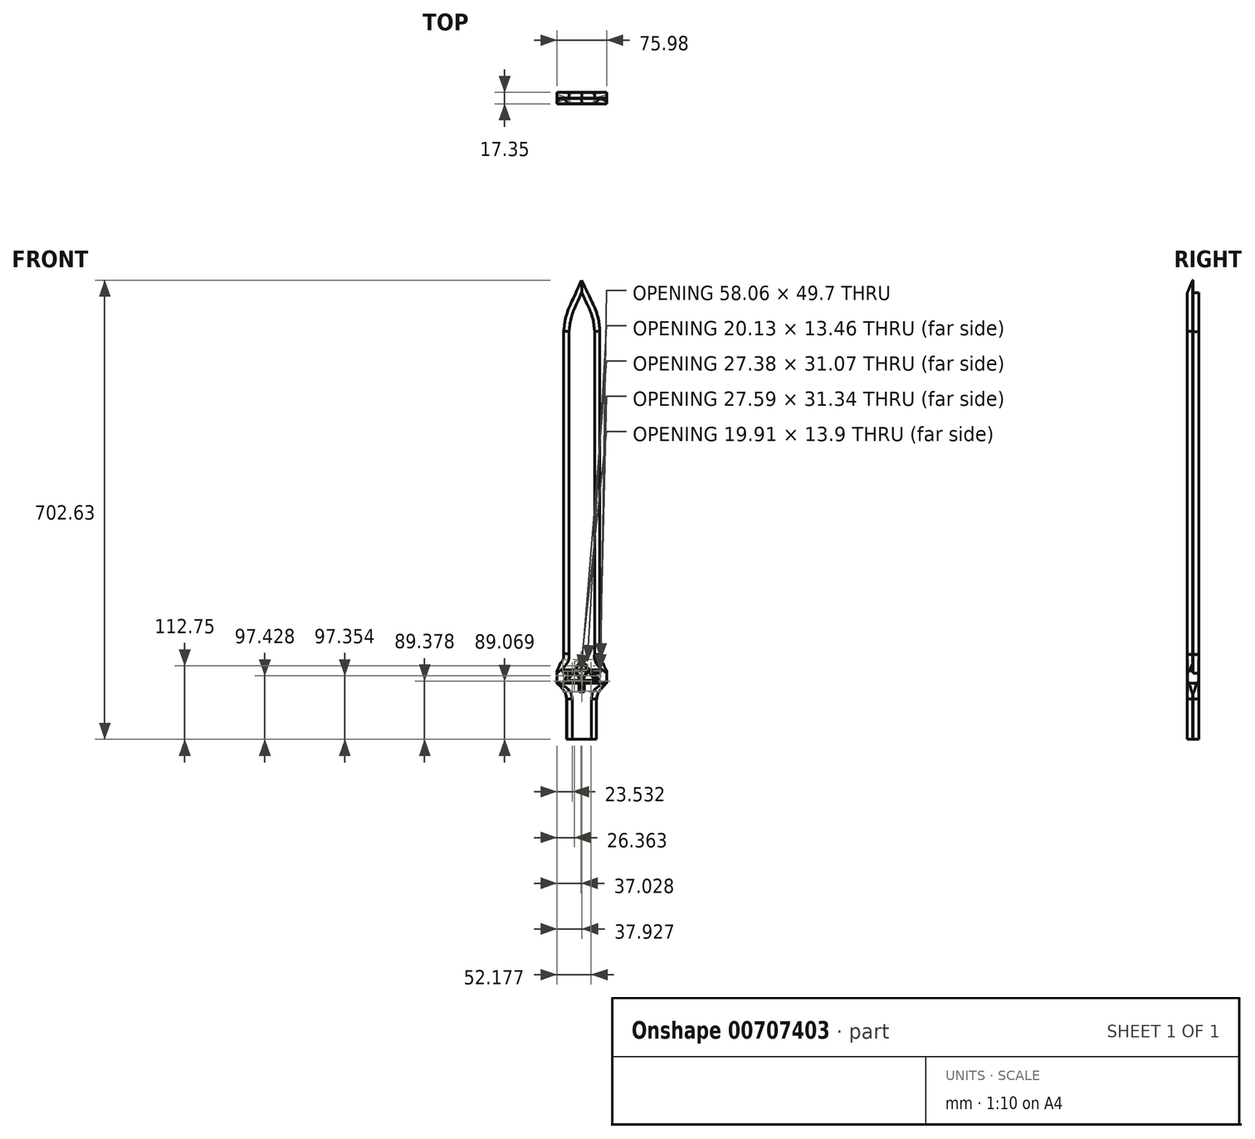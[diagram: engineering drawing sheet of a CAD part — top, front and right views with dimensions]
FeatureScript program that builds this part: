
annotation { "Feature Type Name" : "Feature", "Feature Type Description" : "" }
export const myFeature = defineFeature(function(context is Context, id is Id, definition is map)
    precondition{}
    {
        {
            var Q0;
            Q0=qCreatedBy(makeId("Front.planeOp"),FACE);
            var sketch = newSketch(context, id + "F0", { "sketchPlane" : qUnion([Q0])});
            skLineSegment(sketch, "E0", {"start": v(-23.18, 89.36) * mm, "end": v(-23.18, 27.94) * mm});
            skLineSegment(sketch, "E1", {"start": v(-23.18, 27.94) * mm, "end": v(22.75, 27.94) * mm});
            skLineSegment(sketch, "E2", {"start": v(22.75, 27.94) * mm, "end": v(22.75, 89.36) * mm});
            skFitSpline(sketch, "E3", {"points": [v(-23.18, 89.36) * mm, v(-25.2, 98.78) * mm, v(-29.58, 105.34) * mm, v(-34.12, 110.56) * mm, v(-37.82, 114.26) * mm], "startDerivative": vector(-4.45, 34.79) * mm, "endDerivative": vector(-17.26, 16.67) * mm});
            skFitSpline(sketch, "E4", {"points": [v(22.75, 89.36) * mm, v(24.94, 98.27) * mm, v(29.82, 105.5) * mm, v(34.53, 110.56) * mm, v(38.16, 114.22) * mm], "startDerivative": vector(5.26, 33.12) * mm, "endDerivative": vector(16.94, 16.97) * mm});
            skLineSegment(sketch, "E5", {"start": v(-37.82, 114.26) * mm, "end": v(-37.82, 132.92) * mm});
            skLineSegment(sketch, "E6", {"start": v(38.16, 114.22) * mm, "end": v(38.16, 132.92) * mm});
            skFitSpline(sketch, "E7", {"points": [v(-37.82, 132.92) * mm, v(-34.87, 138.92) * mm, v(-32.96, 144.16) * mm, v(-31.8, 152.09) * mm, v(-31.68, 159) * mm], "startDerivative": vector(12.58, 24.9) * mm, "endDerivative": vector(-0.2, 26.4) * mm});
            skFitSpline(sketch, "E8", {"points": [v(38.16, 132.92) * mm, v(35.43, 137.9) * mm, v(32.87, 144.8) * mm, v(31.98, 152.47) * mm, v(31.85, 157.97) * mm], "startDerivative": vector(-11.86, 20.42) * mm, "endDerivative": vector(-0.27, 22.84) * mm});
            skLineSegment(sketch, "E9", {"start": v(-31.68, 159) * mm, "end": v(-31.68, 655.53) * mm});
            skLineSegment(sketch, "E10", {"start": v(31.85, 157.97) * mm, "end": v(31.87, 655.53) * mm});
            skFitSpline(sketch, "E11", {"points": [v(0, 770.67) * mm, v(5.75, 755.45) * mm, v(13.9, 732.8) * mm, v(20.44, 712.09) * mm, v(27.87, 687.66) * mm, v(30.7, 671.38) * mm, v(31.87, 655.53) * mm], "startDerivative": vector(35.97, -94.67) * mm, "endDerivative": vector(6.36, -107.63) * mm});
            skFitSpline(sketch, "E12", {"points": [v(0, 770.67) * mm, v(-7.17, 751.02) * mm, v(-17.08, 723.77) * mm, v(-25.22, 697.22) * mm, v(-28.94, 682) * mm, v(-31.68, 655.53) * mm], "startDerivative": vector(-36.3, -100.65) * mm, "endDerivative": vector(-10.82, -136.16) * mm});
            skSolve(sketch);
        }
        {
            var Q0;
            Q0=makeQuery(id+"F0.imprint","IMPRINT",FACE,{"disambiguationData":[TD([[makeQuery(id+"F0.imprint","IMPRINT",EDGE,{"derivedFrom":sQuery(id+"F0.wireOp",EDGE,"E0")}),1.0]])]});
            extrude(context, id + "F1", {"entities" : qUnion([Q0]), "depth" : 0.25 * mm, "offsetDistance" : 25.4 * mm});
        }
        {
            var Q0;
            Q0=makeQuery(id+"F1.opExtrude","CAP_FACE",FACE,{"disambiguationData":[OSD([sQuery(id+"F0.wireOp",EDGE,"E0"),sQuery(id+"F0.wireOp",EDGE,"E1"),sQuery(id+"F0.wireOp",EDGE,"E2"),sQuery(id+"F0.wireOp",EDGE,"E3"),sQuery(id+"F0.wireOp",EDGE,"E4"),sQuery(id+"F0.wireOp",EDGE,"E5"),sQuery(id+"F0.wireOp",EDGE,"E6"),sQuery(id+"F0.wireOp",EDGE,"E7"),sQuery(id+"F0.wireOp",EDGE,"E8"),sQuery(id+"F0.wireOp",EDGE,"E9"),sQuery(id+"F0.wireOp",EDGE,"E10"),sQuery(id+"F0.wireOp",EDGE,"E11"),sQuery(id+"F0.wireOp",EDGE,"E12")])],"isStart":true});
            extrude(context, id + "F2", {"entities" : qUnion([Q0]), "operationType" : NewBodyOperationType.ADD, "depth" : 0.25 * mm, "offsetDistance" : 25.4 * mm});
        }
        {
            var Q0;
            Q0=makeQuery(id+"F2.opExtrude","CAP_FACE",FACE,{"disambiguationData":[OSD([sQuery(id+"F0.wireOp",EDGE,"E0"),sQuery(id+"F0.wireOp",EDGE,"E1"),sQuery(id+"F0.wireOp",EDGE,"E2"),sQuery(id+"F0.wireOp",EDGE,"E3"),sQuery(id+"F0.wireOp",EDGE,"E4"),sQuery(id+"F0.wireOp",EDGE,"E5"),sQuery(id+"F0.wireOp",EDGE,"E6"),sQuery(id+"F0.wireOp",EDGE,"E7"),sQuery(id+"F0.wireOp",EDGE,"E8"),sQuery(id+"F0.wireOp",EDGE,"E9"),sQuery(id+"F0.wireOp",EDGE,"E10"),sQuery(id+"F0.wireOp",EDGE,"E11"),sQuery(id+"F0.wireOp",EDGE,"E12")])],"isStart":false});
            var sketch = newSketch(context, id + "F3", { "sketchPlane" : qUnion([Q0])});
            skLineSegment(sketch, "E13", {"start": v(-14.88, 27.94) * mm, "end": v(-14.88, 90.23) * mm});
            skFitSpline(sketch, "E14", {"points": [v(-14.88, 90.23) * mm, v(-16.73, 99.87) * mm, v(-22.43, 106.47) * mm, v(-31.13, 113.07) * mm, v(-38.16, 117.57) * mm], "startDerivative": vector(-3.35, 40.52) * mm, "endDerivative": vector(-28.93, 17.8) * mm});
            skLineSegment(sketch, "E15", {"start": v(14.47, 27.94) * mm, "end": v(14.47, 90.23) * mm});
            skFitSpline(sketch, "E16", {"points": [v(14.47, 90.23) * mm, v(16.95, 99.87) * mm, v(22.69, 106.47) * mm, v(31.86, 113.07) * mm, v(37.82, 117.57) * mm], "startDerivative": vector(6.55, 39.9) * mm, "endDerivative": vector(24.56, 19.23) * mm});
            skFitSpline(sketch, "E17", {"points": [v(37.82, 129.66) * mm, v(28.49, 136.84) * mm, v(22.69, 144.12) * mm, v(19.73, 151.4) * mm, v(19.42, 158.88) * mm], "startDerivative": vector(-34.92, 24.3) * mm, "endDerivative": vector(1.06, 33.21) * mm});
            skFitSpline(sketch, "E18", {"points": [v(-38.16, 129.14) * mm, v(-30.17, 135.78) * mm, v(-23.73, 142.32) * mm, v(-20.88, 147.8) * mm, v(-19.51, 153.3) * mm, v(-19.62, 158.04) * mm], "startDerivative": vector(33.35, 27.05) * mm, "endDerivative": vector(-2.46, 28.44) * mm});
            skLineSegment(sketch, "E19", {"start": v(-19.62, 158.04) * mm, "end": v(-19.62, 652.03) * mm});
            skLineSegment(sketch, "E20", {"start": v(19.42, 158.88) * mm, "end": v(19.33, 652.03) * mm});
            skFitSpline(sketch, "E21", {"points": [v(19.33, 652.03) * mm, v(15.9, 673.87) * mm, v(8.12, 693.88) * mm, v(0, 711.54) * mm], "startDerivative": vector(-6.72, 64.73) * mm, "endDerivative": vector(-25.08, 54.21) * mm});
            skFitSpline(sketch, "E22", {"points": [v(-19.62, 652.03) * mm, v(-16.6, 673.4) * mm, v(-8.12, 694.59) * mm, v(0, 711.54) * mm], "startDerivative": vector(4.95, 63.37) * mm, "endDerivative": vector(25.12, 52.1) * mm});
            skSolve(sketch);
        }
        {
            var Q0;
            {var subQ4=sQuery(id+"F3.wireOp",EDGE,"E13");Q0=makeQuery(id+"F3.imprint","IMPRINT",FACE,{"disambiguationData":[TD([[makeQuery(id+"F3.imprint","IMPRINT",EDGE,{"derivedFrom":subQ4}),-1.0]])]});}
            extrude(context, id + "F4", {"entities" : qUnion([Q0]), "operationType" : NewBodyOperationType.ADD, "depth" : 12.7 * mm, "offsetDistance" : 25.4 * mm});
        }
        {
            var Q0;
            Q0=makeQuery(id+"F4.opExtrude","CAP_FACE",FACE,{"disambiguationData":[OSD([sQuery(id+"F0.wireOp",EDGE,"E1"),sQuery(id+"F0.wireOp",EDGE,"E5"),sQuery(id+"F0.wireOp",EDGE,"E6"),sQuery(id+"F3.wireOp",EDGE,"E13"),sQuery(id+"F3.wireOp",EDGE,"E14"),sQuery(id+"F3.wireOp",EDGE,"E15"),sQuery(id+"F3.wireOp",EDGE,"E16"),sQuery(id+"F3.wireOp",EDGE,"E17"),sQuery(id+"F3.wireOp",EDGE,"E18"),sQuery(id+"F3.wireOp",EDGE,"E19"),sQuery(id+"F3.wireOp",EDGE,"E20"),sQuery(id+"F3.wireOp",EDGE,"E21"),sQuery(id+"F3.wireOp",EDGE,"E22")])],"isStart":false});
            extrude(context, id + "F5", {"entities" : qUnion([Q0]), "operationType" : NewBodyOperationType.ADD, "oppositeDirection" : true, "depth" : 25.9 * mm, "offsetDistance" : 25.4 * mm});
        }
        {
            var Q0;
            Q0=makeQuery(id+"F4.opExtrude","CAP_EDGE",EDGE,{"disambiguationData":[OSD([sQuery(id+"F3.wireOp",EDGE,"E22")])],"isStart":true});
            var Q1;
            Q1=makeQuery(id+"F4.opExtrude","CAP_EDGE",EDGE,{"disambiguationData":[OSD([sQuery(id+"F3.wireOp",EDGE,"E19")])],"isStart":true});
            var Q2;
            Q2=makeQuery(id+"F4.opExtrude","CAP_EDGE",EDGE,{"disambiguationData":[OSD([sQuery(id+"F3.wireOp",EDGE,"E21")])],"isStart":true});
            var Q3;
            Q3=makeQuery(id+"F4.opExtrude","CAP_EDGE",EDGE,{"disambiguationData":[OSD([sQuery(id+"F3.wireOp",EDGE,"E20")])],"isStart":true});
            var Q4;
            Q4=makeQuery(id+"F4.opExtrude","CAP_EDGE",EDGE,{"disambiguationData":[OSD([sQuery(id+"F3.wireOp",EDGE,"E17")])],"isStart":true});
            var Q5;
            Q5=makeQuery(id+"F4.opExtrude","CAP_EDGE",EDGE,{"disambiguationData":[OSD([sQuery(id+"F3.wireOp",EDGE,"E18")])],"isStart":true});
            var Q6;
            Q6=makeQuery(id+"F4.opExtrude","CAP_EDGE",EDGE,{"disambiguationData":[OSD([sQuery(id+"F3.wireOp",EDGE,"E14")])],"isStart":true});
            var Q7;
            Q7=makeQuery(id+"F4.opExtrude","CAP_EDGE",EDGE,{"disambiguationData":[OSD([sQuery(id+"F3.wireOp",EDGE,"E16")])],"isStart":true});
            var Q8;
            Q8=makeQuery(id+"F4.opExtrude","CAP_EDGE",EDGE,{"disambiguationData":[OSD([sQuery(id+"F3.wireOp",EDGE,"E15")])],"isStart":true});
            var Q9;
            Q9=makeQuery(id+"F4.opExtrude","CAP_EDGE",EDGE,{"disambiguationData":[OSD([sQuery(id+"F3.wireOp",EDGE,"E13")])],"isStart":true});
            chamfer(context, id + "F6", {"entities" : qUnion([Q0, Q1, Q2, Q3, Q4, Q5, Q6, Q7, Q8, Q9]), "chamferType" : ChamferType.OFFSET_ANGLE, "width" : 8.13 * mm, "oppositeDirection" : false, "angle" : 47 * degree, "tangentPropagation" : true});
        }
        {
            var Q0;
            Q0=makeQuery(id+"F5.boolean.opBoolean","INTERSECT",EDGE,{"derivedFrom":[makeQuery(id+"F1.opExtrude","CAP_FACE",FACE,{"disambiguationData":[OSD([sQuery(id+"F0.wireOp",EDGE,"E0"),sQuery(id+"F0.wireOp",EDGE,"E1"),sQuery(id+"F0.wireOp",EDGE,"E2"),sQuery(id+"F0.wireOp",EDGE,"E3"),sQuery(id+"F0.wireOp",EDGE,"E4"),sQuery(id+"F0.wireOp",EDGE,"E5"),sQuery(id+"F0.wireOp",EDGE,"E6"),sQuery(id+"F0.wireOp",EDGE,"E7"),sQuery(id+"F0.wireOp",EDGE,"E8"),sQuery(id+"F0.wireOp",EDGE,"E9"),sQuery(id+"F0.wireOp",EDGE,"E10"),sQuery(id+"F0.wireOp",EDGE,"E11"),sQuery(id+"F0.wireOp",EDGE,"E12")])],"isStart":false}),makeQuery(id+"F5.opExtrude","SWEPT_FACE",FACE,{"disambiguationData":[OSD([sQuery(id+"F3.wireOp",EDGE,"E20")])]})]});
            var Q1;
            Q1=makeQuery(id+"F5.boolean.opBoolean","INTERSECT",EDGE,{"derivedFrom":[makeQuery(id+"F1.opExtrude","CAP_FACE",FACE,{"disambiguationData":[OSD([sQuery(id+"F0.wireOp",EDGE,"E0"),sQuery(id+"F0.wireOp",EDGE,"E1"),sQuery(id+"F0.wireOp",EDGE,"E2"),sQuery(id+"F0.wireOp",EDGE,"E3"),sQuery(id+"F0.wireOp",EDGE,"E4"),sQuery(id+"F0.wireOp",EDGE,"E5"),sQuery(id+"F0.wireOp",EDGE,"E6"),sQuery(id+"F0.wireOp",EDGE,"E7"),sQuery(id+"F0.wireOp",EDGE,"E8"),sQuery(id+"F0.wireOp",EDGE,"E9"),sQuery(id+"F0.wireOp",EDGE,"E10"),sQuery(id+"F0.wireOp",EDGE,"E11"),sQuery(id+"F0.wireOp",EDGE,"E12")])],"isStart":false}),makeQuery(id+"F5.opExtrude","SWEPT_FACE",FACE,{"disambiguationData":[OSD([sQuery(id+"F3.wireOp",EDGE,"E17")])]})]});
            var Q2;
            Q2=makeQuery(id+"F5.boolean.opBoolean","INTERSECT",EDGE,{"derivedFrom":[makeQuery(id+"F1.opExtrude","CAP_FACE",FACE,{"disambiguationData":[OSD([sQuery(id+"F0.wireOp",EDGE,"E0"),sQuery(id+"F0.wireOp",EDGE,"E1"),sQuery(id+"F0.wireOp",EDGE,"E2"),sQuery(id+"F0.wireOp",EDGE,"E3"),sQuery(id+"F0.wireOp",EDGE,"E4"),sQuery(id+"F0.wireOp",EDGE,"E5"),sQuery(id+"F0.wireOp",EDGE,"E6"),sQuery(id+"F0.wireOp",EDGE,"E7"),sQuery(id+"F0.wireOp",EDGE,"E8"),sQuery(id+"F0.wireOp",EDGE,"E9"),sQuery(id+"F0.wireOp",EDGE,"E10"),sQuery(id+"F0.wireOp",EDGE,"E11"),sQuery(id+"F0.wireOp",EDGE,"E12")])],"isStart":false}),makeQuery(id+"F5.opExtrude","SWEPT_FACE",FACE,{"disambiguationData":[OSD([sQuery(id+"F3.wireOp",EDGE,"E16")])]})]});
            var Q3;
            Q3=makeQuery(id+"F5.boolean.opBoolean","INTERSECT",EDGE,{"derivedFrom":[makeQuery(id+"F1.opExtrude","CAP_FACE",FACE,{"disambiguationData":[OSD([sQuery(id+"F0.wireOp",EDGE,"E0"),sQuery(id+"F0.wireOp",EDGE,"E1"),sQuery(id+"F0.wireOp",EDGE,"E2"),sQuery(id+"F0.wireOp",EDGE,"E3"),sQuery(id+"F0.wireOp",EDGE,"E4"),sQuery(id+"F0.wireOp",EDGE,"E5"),sQuery(id+"F0.wireOp",EDGE,"E6"),sQuery(id+"F0.wireOp",EDGE,"E7"),sQuery(id+"F0.wireOp",EDGE,"E8"),sQuery(id+"F0.wireOp",EDGE,"E9"),sQuery(id+"F0.wireOp",EDGE,"E10"),sQuery(id+"F0.wireOp",EDGE,"E11"),sQuery(id+"F0.wireOp",EDGE,"E12")])],"isStart":false}),makeQuery(id+"F5.opExtrude","SWEPT_FACE",FACE,{"disambiguationData":[OSD([sQuery(id+"F3.wireOp",EDGE,"E15")])]})]});
            var Q4;
            Q4=makeQuery(id+"F5.boolean.opBoolean","INTERSECT",EDGE,{"derivedFrom":[makeQuery(id+"F1.opExtrude","CAP_FACE",FACE,{"disambiguationData":[OSD([sQuery(id+"F0.wireOp",EDGE,"E0"),sQuery(id+"F0.wireOp",EDGE,"E1"),sQuery(id+"F0.wireOp",EDGE,"E2"),sQuery(id+"F0.wireOp",EDGE,"E3"),sQuery(id+"F0.wireOp",EDGE,"E4"),sQuery(id+"F0.wireOp",EDGE,"E5"),sQuery(id+"F0.wireOp",EDGE,"E6"),sQuery(id+"F0.wireOp",EDGE,"E7"),sQuery(id+"F0.wireOp",EDGE,"E8"),sQuery(id+"F0.wireOp",EDGE,"E9"),sQuery(id+"F0.wireOp",EDGE,"E10"),sQuery(id+"F0.wireOp",EDGE,"E11"),sQuery(id+"F0.wireOp",EDGE,"E12")])],"isStart":false}),makeQuery(id+"F5.opExtrude","SWEPT_FACE",FACE,{"disambiguationData":[OSD([sQuery(id+"F3.wireOp",EDGE,"E13")])]})]});
            var Q5;
            Q5=makeQuery(id+"F5.boolean.opBoolean","INTERSECT",EDGE,{"derivedFrom":[makeQuery(id+"F1.opExtrude","CAP_FACE",FACE,{"disambiguationData":[OSD([sQuery(id+"F0.wireOp",EDGE,"E0"),sQuery(id+"F0.wireOp",EDGE,"E1"),sQuery(id+"F0.wireOp",EDGE,"E2"),sQuery(id+"F0.wireOp",EDGE,"E3"),sQuery(id+"F0.wireOp",EDGE,"E4"),sQuery(id+"F0.wireOp",EDGE,"E5"),sQuery(id+"F0.wireOp",EDGE,"E6"),sQuery(id+"F0.wireOp",EDGE,"E7"),sQuery(id+"F0.wireOp",EDGE,"E8"),sQuery(id+"F0.wireOp",EDGE,"E9"),sQuery(id+"F0.wireOp",EDGE,"E10"),sQuery(id+"F0.wireOp",EDGE,"E11"),sQuery(id+"F0.wireOp",EDGE,"E12")])],"isStart":false}),makeQuery(id+"F5.opExtrude","SWEPT_FACE",FACE,{"disambiguationData":[OSD([sQuery(id+"F3.wireOp",EDGE,"E14")])]})]});
            var Q6;
            Q6=makeQuery(id+"F5.boolean.opBoolean","INTERSECT",EDGE,{"derivedFrom":[makeQuery(id+"F1.opExtrude","CAP_FACE",FACE,{"disambiguationData":[OSD([sQuery(id+"F0.wireOp",EDGE,"E0"),sQuery(id+"F0.wireOp",EDGE,"E1"),sQuery(id+"F0.wireOp",EDGE,"E2"),sQuery(id+"F0.wireOp",EDGE,"E3"),sQuery(id+"F0.wireOp",EDGE,"E4"),sQuery(id+"F0.wireOp",EDGE,"E5"),sQuery(id+"F0.wireOp",EDGE,"E6"),sQuery(id+"F0.wireOp",EDGE,"E7"),sQuery(id+"F0.wireOp",EDGE,"E8"),sQuery(id+"F0.wireOp",EDGE,"E9"),sQuery(id+"F0.wireOp",EDGE,"E10"),sQuery(id+"F0.wireOp",EDGE,"E11"),sQuery(id+"F0.wireOp",EDGE,"E12")])],"isStart":false}),makeQuery(id+"F5.opExtrude","SWEPT_FACE",FACE,{"disambiguationData":[OSD([sQuery(id+"F3.wireOp",EDGE,"E18")])]})]});
            var Q7;
            Q7=makeQuery(id+"F5.boolean.opBoolean","INTERSECT",EDGE,{"derivedFrom":[makeQuery(id+"F1.opExtrude","CAP_FACE",FACE,{"disambiguationData":[OSD([sQuery(id+"F0.wireOp",EDGE,"E0"),sQuery(id+"F0.wireOp",EDGE,"E1"),sQuery(id+"F0.wireOp",EDGE,"E2"),sQuery(id+"F0.wireOp",EDGE,"E3"),sQuery(id+"F0.wireOp",EDGE,"E4"),sQuery(id+"F0.wireOp",EDGE,"E5"),sQuery(id+"F0.wireOp",EDGE,"E6"),sQuery(id+"F0.wireOp",EDGE,"E7"),sQuery(id+"F0.wireOp",EDGE,"E8"),sQuery(id+"F0.wireOp",EDGE,"E9"),sQuery(id+"F0.wireOp",EDGE,"E10"),sQuery(id+"F0.wireOp",EDGE,"E11"),sQuery(id+"F0.wireOp",EDGE,"E12")])],"isStart":false}),makeQuery(id+"F5.opExtrude","SWEPT_FACE",FACE,{"disambiguationData":[OSD([sQuery(id+"F3.wireOp",EDGE,"E19")])]})]});
            var Q8;
            Q8=makeQuery(id+"F5.boolean.opBoolean","INTERSECT",EDGE,{"derivedFrom":[makeQuery(id+"F1.opExtrude","CAP_FACE",FACE,{"disambiguationData":[OSD([sQuery(id+"F0.wireOp",EDGE,"E0"),sQuery(id+"F0.wireOp",EDGE,"E1"),sQuery(id+"F0.wireOp",EDGE,"E2"),sQuery(id+"F0.wireOp",EDGE,"E3"),sQuery(id+"F0.wireOp",EDGE,"E4"),sQuery(id+"F0.wireOp",EDGE,"E5"),sQuery(id+"F0.wireOp",EDGE,"E6"),sQuery(id+"F0.wireOp",EDGE,"E7"),sQuery(id+"F0.wireOp",EDGE,"E8"),sQuery(id+"F0.wireOp",EDGE,"E9"),sQuery(id+"F0.wireOp",EDGE,"E10"),sQuery(id+"F0.wireOp",EDGE,"E11"),sQuery(id+"F0.wireOp",EDGE,"E12")])],"isStart":false}),makeQuery(id+"F5.opExtrude","SWEPT_FACE",FACE,{"disambiguationData":[OSD([sQuery(id+"F3.wireOp",EDGE,"E22")])]})]});
            var Q9;
            Q9=makeQuery(id+"F5.boolean.opBoolean","INTERSECT",EDGE,{"derivedFrom":[makeQuery(id+"F1.opExtrude","CAP_FACE",FACE,{"disambiguationData":[OSD([sQuery(id+"F0.wireOp",EDGE,"E0"),sQuery(id+"F0.wireOp",EDGE,"E1"),sQuery(id+"F0.wireOp",EDGE,"E2"),sQuery(id+"F0.wireOp",EDGE,"E3"),sQuery(id+"F0.wireOp",EDGE,"E4"),sQuery(id+"F0.wireOp",EDGE,"E5"),sQuery(id+"F0.wireOp",EDGE,"E6"),sQuery(id+"F0.wireOp",EDGE,"E7"),sQuery(id+"F0.wireOp",EDGE,"E8"),sQuery(id+"F0.wireOp",EDGE,"E9"),sQuery(id+"F0.wireOp",EDGE,"E10"),sQuery(id+"F0.wireOp",EDGE,"E11"),sQuery(id+"F0.wireOp",EDGE,"E12")])],"isStart":false}),makeQuery(id+"F5.opExtrude","SWEPT_FACE",FACE,{"disambiguationData":[OSD([sQuery(id+"F3.wireOp",EDGE,"E21")])]})]});
            chamfer(context, id + "F7", {"entities" : qUnion([Q0, Q1, Q2, Q3, Q4, Q5, Q6, Q7, Q8, Q9]), "width" : 8.13 * mm, "tangentPropagation" : true});
        }
        {
            var Q0;
            Q0=makeQuery(id+"F5.opExtrude","CAP_FACE",FACE,{"disambiguationData":[OSD([sQuery(id+"F0.wireOp",EDGE,"E1"),sQuery(id+"F0.wireOp",EDGE,"E5"),sQuery(id+"F0.wireOp",EDGE,"E6"),sQuery(id+"F3.wireOp",EDGE,"E13"),sQuery(id+"F3.wireOp",EDGE,"E14"),sQuery(id+"F3.wireOp",EDGE,"E15"),sQuery(id+"F3.wireOp",EDGE,"E16"),sQuery(id+"F3.wireOp",EDGE,"E17"),sQuery(id+"F3.wireOp",EDGE,"E18"),sQuery(id+"F3.wireOp",EDGE,"E19"),sQuery(id+"F3.wireOp",EDGE,"E20"),sQuery(id+"F3.wireOp",EDGE,"E21"),sQuery(id+"F3.wireOp",EDGE,"E22")])],"isStart":false});
            extrude(context, id + "F8", {"entities" : qUnion([Q0]), "operationType" : NewBodyOperationType.REMOVE, "oppositeDirection" : true, "depth" : 5.33 * mm, "offsetDistance" : 25.4 * mm});
        }
        {
            var Q0;
            Q0=makeQuery(id+"F4.opExtrude","CAP_FACE",FACE,{"disambiguationData":[OSD([sQuery(id+"F0.wireOp",EDGE,"E1"),sQuery(id+"F0.wireOp",EDGE,"E5"),sQuery(id+"F0.wireOp",EDGE,"E6"),sQuery(id+"F3.wireOp",EDGE,"E13"),sQuery(id+"F3.wireOp",EDGE,"E14"),sQuery(id+"F3.wireOp",EDGE,"E15"),sQuery(id+"F3.wireOp",EDGE,"E16"),sQuery(id+"F3.wireOp",EDGE,"E17"),sQuery(id+"F3.wireOp",EDGE,"E18"),sQuery(id+"F3.wireOp",EDGE,"E19"),sQuery(id+"F3.wireOp",EDGE,"E20"),sQuery(id+"F3.wireOp",EDGE,"E21"),sQuery(id+"F3.wireOp",EDGE,"E22")])],"isStart":false});
            extrude(context, id + "F9", {"entities" : qUnion([Q0]), "operationType" : NewBodyOperationType.REMOVE, "oppositeDirection" : true, "depth" : 4 * mm, "offsetDistance" : 25.4 * mm});
        }
        {
            var Q0;
            {var subQ0=sQuery(id+"F0.wireOp",EDGE,"E12");var subQ1=sQuery(id+"F0.wireOp",EDGE,"E11");var subQ2=sQuery(id+"F0.wireOp",EDGE,"E10");var subQ3=sQuery(id+"F0.wireOp",EDGE,"E9");var subQ4=sQuery(id+"F0.wireOp",EDGE,"E8");var subQ5=sQuery(id+"F0.wireOp",EDGE,"E7");var subQ6=sQuery(id+"F0.wireOp",EDGE,"E6");var subQ7=sQuery(id+"F0.wireOp",EDGE,"E5");Q0=makeQuery(id+"F5.boolean.opBoolean","SPLIT",FACE,{"disambiguationData":[TD([makeQuery(id+"F1.opExtrude","SWEPT_FACE",FACE,{"disambiguationData":[OSD([subQ5])]})])],"derivedFrom":makeQuery(id+"F1.opExtrude","CAP_FACE",FACE,{"disambiguationData":[OSD([sQuery(id+"F0.wireOp",EDGE,"E0"),sQuery(id+"F0.wireOp",EDGE,"E1"),sQuery(id+"F0.wireOp",EDGE,"E2"),sQuery(id+"F0.wireOp",EDGE,"E3"),sQuery(id+"F0.wireOp",EDGE,"E4"),subQ7,subQ6,subQ5,subQ4,subQ3,subQ2,subQ1,subQ0])],"isStart":false})});}
            extrude(context, id + "F10", {"entities" : qUnion([Q0]), "operationType" : NewBodyOperationType.REMOVE, "oppositeDirection" : true, "depth" : 25.4 * mm, "offsetDistance" : 25.4 * mm});
        }
        {
            var Q0;
            Q0=makeQuery(id+"F8.boolean.opBoolean","COPY",FACE,{"derivedFrom":makeQuery(id+"F8.opExtrude","CAP_FACE",FACE,{"disambiguationData":[OSD([sQuery(id+"F0.wireOp",EDGE,"E1"),sQuery(id+"F0.wireOp",EDGE,"E5"),sQuery(id+"F0.wireOp",EDGE,"E6"),sQuery(id+"F3.wireOp",EDGE,"E13"),sQuery(id+"F3.wireOp",EDGE,"E14"),sQuery(id+"F3.wireOp",EDGE,"E15"),sQuery(id+"F3.wireOp",EDGE,"E16"),sQuery(id+"F3.wireOp",EDGE,"E17"),sQuery(id+"F3.wireOp",EDGE,"E18"),sQuery(id+"F3.wireOp",EDGE,"E19"),sQuery(id+"F3.wireOp",EDGE,"E20"),sQuery(id+"F3.wireOp",EDGE,"E21"),sQuery(id+"F3.wireOp",EDGE,"E22")])],"isStart":false})});
            extrude(context, id + "F11", {"entities" : qUnion([Q0]), "operationType" : NewBodyOperationType.ADD, "depth" : 0.76 * mm, "offsetDistance" : 25.4 * mm});
        }
        {
            var Q0;
            Q0=makeQuery(id+"F9.boolean.opBoolean","COPY",FACE,{"derivedFrom":makeQuery(id+"F9.opExtrude","CAP_FACE",FACE,{"disambiguationData":[OSD([sQuery(id+"F0.wireOp",EDGE,"E1"),sQuery(id+"F0.wireOp",EDGE,"E5"),sQuery(id+"F0.wireOp",EDGE,"E6"),sQuery(id+"F3.wireOp",EDGE,"E13"),sQuery(id+"F3.wireOp",EDGE,"E14"),sQuery(id+"F3.wireOp",EDGE,"E15"),sQuery(id+"F3.wireOp",EDGE,"E16"),sQuery(id+"F3.wireOp",EDGE,"E17"),sQuery(id+"F3.wireOp",EDGE,"E18"),sQuery(id+"F3.wireOp",EDGE,"E19"),sQuery(id+"F3.wireOp",EDGE,"E20"),sQuery(id+"F3.wireOp",EDGE,"E21"),sQuery(id+"F3.wireOp",EDGE,"E22")])],"isStart":false})});
            var sketch = newSketch(context, id + "F12", { "sketchPlane" : qUnion([Q0])});
            skLineSegment(sketch, "E23", {"start": v(-11.79, 134.23) * mm, "end": v(0, 150.22) * mm});
            skLineSegment(sketch, "E24", {"start": v(0, 150.22) * mm, "end": v(12.06, 133.96) * mm});
            skLineSegment(sketch, "E25", {"start": v(12.06, 133.96) * mm, "end": v(26.89, 133.96) * mm});
            skLineSegment(sketch, "E26", {"start": v(26.89, 129.23) * mm, "end": v(19.36, 129.23) * mm});
            skLineSegment(sketch, "E27", {"start": v(19.36, 129.23) * mm, "end": v(27.93, 116.9) * mm});
            skLineSegment(sketch, "E28", {"start": v(26.89, 114) * mm, "end": v(4.81, 114) * mm});
            skLineSegment(sketch, "E29", {"start": v(-5.35, 114) * mm, "end": v(-27.24, 114) * mm});
            skLineSegment(sketch, "E30", {"start": v(-27.9, 116.9) * mm, "end": v(-19.08, 129.43) * mm});
            skLineSegment(sketch, "E31", {"start": v(-19.08, 129.43) * mm, "end": v(-27.24, 129.43) * mm});
            skLineSegment(sketch, "E32", {"start": v(-11.79, 134.23) * mm, "end": v(-27.24, 134.23) * mm});
            skLineSegment(sketch, "E33", {"start": v(0, 147.42) * mm, "end": v(-9.27, 134.23) * mm});
            skLineSegment(sketch, "E34", {"start": v(-9.27, 134.23) * mm, "end": v(10.86, 133.96) * mm});
            skLineSegment(sketch, "E35", {"start": v(10.86, 133.96) * mm, "end": v(0, 147.42) * mm});
            skLineSegment(sketch, "E36", {"start": v(-11.79, 132.99) * mm, "end": v(-21.8, 119.4) * mm});
            skLineSegment(sketch, "E37", {"start": v(-21.25, 117.57) * mm, "end": v(-0.56, 117.57) * mm});
            skLineSegment(sketch, "E38", {"start": v(-0.56, 117.57) * mm, "end": v(-0.56, 102.3) * mm});
            skLineSegment(sketch, "E39", {"start": v(-4.22, 102.3) * mm, "end": v(-4.22, 113.14) * mm});
            skLineSegment(sketch, "E40", {"start": v(4.21, 113.14) * mm, "end": v(4.21, 102.3) * mm});
            skLineSegment(sketch, "E41", {"start": v(0.6, 102.3) * mm, "end": v(0.6, 117.57) * mm});
            skLineSegment(sketch, "E42", {"start": v(0.6, 117.57) * mm, "end": v(21.41, 117.57) * mm});
            skLineSegment(sketch, "E43", {"start": v(22.25, 118.83) * mm, "end": v(12.3, 132.54) * mm});
            skLineSegment(sketch, "E44", {"start": v(12.3, 132.54) * mm, "end": v(26.89, 132.54) * mm});
            skLineSegment(sketch, "E45", {"start": v(26.89, 130.12) * mm, "end": v(18.73, 130.12) * mm});
            skLineSegment(sketch, "E46", {"start": v(18.4, 128.97) * mm, "end": v(27.24, 116.24) * mm});
            skLineSegment(sketch, "E47", {"start": v(-20.22, 118.34) * mm, "end": v(-10.53, 132.13) * mm});
            skLineSegment(sketch, "E48", {"start": v(-10.53, 132.13) * mm, "end": v(-0.88, 118.24) * mm});
            skLineSegment(sketch, "E49", {"start": v(-0.88, 118.24) * mm, "end": v(-20.22, 118.34) * mm});
            skLineSegment(sketch, "E50", {"start": v(1.5, 118.34) * mm, "end": v(11.28, 132.25) * mm});
            skLineSegment(sketch, "E51", {"start": v(11.28, 132.25) * mm, "end": v(21.41, 118.34) * mm});
            skLineSegment(sketch, "E52", {"start": v(21.41, 118.34) * mm, "end": v(1.5, 118.34) * mm});
            skLineSegment(sketch, "E53", {"start": v(9.51, 132.94) * mm, "end": v(-9.05, 132.94) * mm});
            skLineSegment(sketch, "E54", {"start": v(-9.05, 132.94) * mm, "end": v(0, 119.04) * mm});
            skLineSegment(sketch, "E55", {"start": v(0, 119.04) * mm, "end": v(9.51, 132.94) * mm});
            skFitSpline(sketch, "E56", {"points": [v(-21.25, 117.57) * mm, v(-22.4, 117.93) * mm, v(-21.8, 119.4) * mm], "startDerivative": vector(-3.32, 0.3) * mm, "endDerivative": vector(2.1, 3.3) * mm});
            skFitSpline(sketch, "E57", {"points": [v(-27.24, 114) * mm, v(-28.28, 115.14) * mm, v(-27.9, 116.9) * mm], "startDerivative": vector(-2.88, 2.13) * mm, "endDerivative": vector(1.5, 3.64) * mm});
            skFitSpline(sketch, "E58", {"points": [v(-27.24, 129.43) * mm, v(-28.9, 130.86) * mm, v(-28.84, 133.23) * mm, v(-27.24, 134.23) * mm], "startDerivative": vector(-5.9, 3.35) * mm, "endDerivative": vector(6.04, 2.14) * mm});
            skFitSpline(sketch, "E59", {"points": [v(22.25, 118.83) * mm, v(22.47, 117.72) * mm, v(21.41, 117.57) * mm], "startDerivative": vector(1.1, -2.67) * mm, "endDerivative": vector(-2.78, 0.17) * mm});
            skLineSegment(sketch, "E60", {"start": v(-11.79, 132.99) * mm, "end": v(-27.37, 132.99) * mm});
            skLineSegment(sketch, "E61", {"start": v(26.7, 114.7) * mm, "end": v(4.81, 114.7) * mm});
            skLineSegment(sketch, "E62", {"start": v(3.19, 113.27) * mm, "end": v(3.38, 102.25) * mm});
            skLineSegment(sketch, "E63", {"start": v(-3, 102.25) * mm, "end": v(-3, 113.23) * mm});
            skLineSegment(sketch, "E64", {"start": v(-5.42, 115.26) * mm, "end": v(-26.92, 115.26) * mm});
            skLineSegment(sketch, "E65", {"start": v(-27.2, 116.42) * mm, "end": v(-18, 129.5) * mm});
            skLineSegment(sketch, "E66", {"start": v(-19.1, 130.43) * mm, "end": v(-27.37, 130.43) * mm});
            skFitSpline(sketch, "E67", {"points": [v(-27.37, 132.99) * mm, v(-28.15, 131.74) * mm, v(-27.37, 130.43) * mm], "startDerivative": vector(-2.36, -2.5) * mm, "endDerivative": vector(2.34, -2.6) * mm});
            skFitSpline(sketch, "E68", {"points": [v(26.89, 133.96) * mm, v(28.5, 132.99) * mm, v(28.73, 130.43) * mm, v(26.89, 129.23) * mm], "startDerivative": vector(5.97, -1.95) * mm, "endDerivative": vector(-6.8, -2.42) * mm});
            skFitSpline(sketch, "E69", {"points": [v(26.89, 130.12) * mm, v(27.98, 131.53) * mm, v(26.89, 132.54) * mm], "startDerivative": vector(3.22, 2.86) * mm, "endDerivative": vector(-3.32, 1.98) * mm});
            skFitSpline(sketch, "E70", {"points": [v(18.73, 130.12) * mm, v(18.23, 129.75) * mm, v(18.4, 128.97) * mm], "startDerivative": vector(-1.4, -0.61) * mm, "endDerivative": vector(0.7, -1.65) * mm});
            skFitSpline(sketch, "E71", {"points": [v(27.24, 116.24) * mm, v(27.43, 115.26) * mm, v(26.7, 114.7) * mm], "startDerivative": vector(0.84, -2.13) * mm, "endDerivative": vector(-1.93, -0.96) * mm});
            skFitSpline(sketch, "E72", {"points": [v(27.93, 116.9) * mm, v(28.3, 115.33) * mm, v(27.7, 114.19) * mm, v(26.89, 114) * mm], "startDerivative": vector(1.64, -4.12) * mm, "endDerivative": vector(-3.1, -0.07) * mm});
            skFitSpline(sketch, "E73", {"points": [v(4.81, 114.7) * mm, v(3.92, 114.6) * mm, v(3.37, 114.15) * mm, v(3.19, 113.27) * mm], "startDerivative": vector(-2.72, 0.02) * mm, "endDerivative": vector(-0.22, -2.76) * mm});
            skFitSpline(sketch, "E74", {"points": [v(4.81, 114) * mm, v(4.22, 113.8) * mm, v(4.21, 113.14) * mm], "startDerivative": vector(-1.5, -0.2) * mm, "endDerivative": vector(0.3, -1.52) * mm});
            skFitSpline(sketch, "E75", {"points": [v(4.21, 102.3) * mm, v(3.38, 100.95) * mm, v(1.67, 100.75) * mm, v(0, 101.38) * mm], "startDerivative": vector(-1.94, -4.96) * mm, "endDerivative": vector(-4.65, 2.26) * mm});
            skFitSpline(sketch, "E76", {"points": [v(0.6, 102.3) * mm, v(1.44, 101.61) * mm, v(2.73, 101.58) * mm, v(3.38, 102.25) * mm], "startDerivative": vector(2.16, -2.4) * mm, "endDerivative": vector(1.66, 2.62) * mm});
            skFitSpline(sketch, "E77", {"points": [v(-0.56, 102.3) * mm, v(-1.1, 101.78) * mm, v(-2.42, 101.75) * mm, v(-3, 102.25) * mm], "startDerivative": vector(-1.33, -2) * mm, "endDerivative": vector(-1.49, 1.96) * mm});
            skFitSpline(sketch, "E78", {"points": [v(0, 101.38) * mm, v(-0.56, 100.71) * mm, v(-3, 100.75) * mm, v(-4.22, 102.3) * mm], "startDerivative": vector(-1.43, -3.14) * mm, "endDerivative": vector(-2.38, 5.15) * mm});
            skFitSpline(sketch, "E79", {"points": [v(-3, 113.23) * mm, v(-3, 114.27) * mm, v(-4.01, 115.29) * mm, v(-5.42, 115.26) * mm], "startDerivative": vector(0.63, 3.44) * mm, "endDerivative": vector(-4.15, -0.82) * mm});
            skFitSpline(sketch, "E80", {"points": [v(-5.35, 114) * mm, v(-4.5, 114) * mm, v(-4.22, 113.14) * mm], "startDerivative": vector(2, 0.42) * mm, "endDerivative": vector(0.26, -2.12) * mm});
            skFitSpline(sketch, "E81", {"points": [v(-26.92, 115.26) * mm, v(-27.37, 115.58) * mm, v(-27.2, 116.42) * mm], "startDerivative": vector(-1.3, 0.54) * mm, "endDerivative": vector(0.67, 1.74) * mm});
            skFitSpline(sketch, "E82", {"points": [v(-19.1, 130.43) * mm, v(-18.31, 130.12) * mm, v(-18, 129.5) * mm], "startDerivative": vector(1.7, -0.42) * mm, "endDerivative": vector(0.44, -1.46) * mm});
            skSolve(sketch);
        }
        {
            var Q0;
            Q0=makeQuery(id+"F12.imprint","IMPRINT",FACE,{"disambiguationData":[TD([[makeQuery(id+"F12.imprint","IMPRINT",EDGE,{"derivedFrom":sQuery(id+"F12.wireOp",EDGE,"E23")}),-1.0]])]});
            extrude(context, id + "F13", {"entities" : qUnion([Q0]), "operationType" : NewBodyOperationType.ADD, "depth" : 12.7 * mm, "offsetDistance" : 25.4 * mm});
        }
        {
            var Q0;
            Q0=makeQuery(id+"F13.opExtrude","CAP_FACE",FACE,{"disambiguationData":[OSD([sQuery(id+"F12.wireOp",EDGE,"E23"),sQuery(id+"F12.wireOp",EDGE,"E24"),sQuery(id+"F12.wireOp",EDGE,"E25"),sQuery(id+"F12.wireOp",EDGE,"E26"),sQuery(id+"F12.wireOp",EDGE,"E27"),sQuery(id+"F12.wireOp",EDGE,"E28"),sQuery(id+"F12.wireOp",EDGE,"E29"),sQuery(id+"F12.wireOp",EDGE,"E30"),sQuery(id+"F12.wireOp",EDGE,"E31"),sQuery(id+"F12.wireOp",EDGE,"E32"),sQuery(id+"F12.wireOp",EDGE,"E33"),sQuery(id+"F12.wireOp",EDGE,"E34"),sQuery(id+"F12.wireOp",EDGE,"E35"),sQuery(id+"F12.wireOp",EDGE,"E36"),sQuery(id+"F12.wireOp",EDGE,"E37"),sQuery(id+"F12.wireOp",EDGE,"E38"),sQuery(id+"F12.wireOp",EDGE,"E39"),sQuery(id+"F12.wireOp",EDGE,"E40"),sQuery(id+"F12.wireOp",EDGE,"E41"),sQuery(id+"F12.wireOp",EDGE,"E42"),sQuery(id+"F12.wireOp",EDGE,"E43"),sQuery(id+"F12.wireOp",EDGE,"E44"),sQuery(id+"F12.wireOp",EDGE,"E45"),sQuery(id+"F12.wireOp",EDGE,"E46"),sQuery(id+"F12.wireOp",EDGE,"E47"),sQuery(id+"F12.wireOp",EDGE,"E48"),sQuery(id+"F12.wireOp",EDGE,"E49"),sQuery(id+"F12.wireOp",EDGE,"E50"),sQuery(id+"F12.wireOp",EDGE,"E51"),sQuery(id+"F12.wireOp",EDGE,"E52"),sQuery(id+"F12.wireOp",EDGE,"E53"),sQuery(id+"F12.wireOp",EDGE,"E54"),sQuery(id+"F12.wireOp",EDGE,"E55"),sQuery(id+"F12.wireOp",EDGE,"E56"),sQuery(id+"F12.wireOp",EDGE,"E57"),sQuery(id+"F12.wireOp",EDGE,"E58"),sQuery(id+"F12.wireOp",EDGE,"E59"),sQuery(id+"F12.wireOp",EDGE,"E60"),sQuery(id+"F12.wireOp",EDGE,"E61"),sQuery(id+"F12.wireOp",EDGE,"E62"),sQuery(id+"F12.wireOp",EDGE,"E63"),sQuery(id+"F12.wireOp",EDGE,"E64"),sQuery(id+"F12.wireOp",EDGE,"E65"),sQuery(id+"F12.wireOp",EDGE,"E66"),sQuery(id+"F12.wireOp",EDGE,"E67"),sQuery(id+"F12.wireOp",EDGE,"E68"),sQuery(id+"F12.wireOp",EDGE,"E69"),sQuery(id+"F12.wireOp",EDGE,"E70"),sQuery(id+"F12.wireOp",EDGE,"E71"),sQuery(id+"F12.wireOp",EDGE,"E72"),sQuery(id+"F12.wireOp",EDGE,"E73"),sQuery(id+"F12.wireOp",EDGE,"E74"),sQuery(id+"F12.wireOp",EDGE,"E75"),sQuery(id+"F12.wireOp",EDGE,"E76"),sQuery(id+"F12.wireOp",EDGE,"E77"),sQuery(id+"F12.wireOp",EDGE,"E78"),sQuery(id+"F12.wireOp",EDGE,"E79"),sQuery(id+"F12.wireOp",EDGE,"E80"),sQuery(id+"F12.wireOp",EDGE,"E81"),sQuery(id+"F12.wireOp",EDGE,"E82")])],"isStart":false});
            extrude(context, id + "F14", {"entities" : qUnion([Q0]), "operationType" : NewBodyOperationType.REMOVE, "oppositeDirection" : true, "depth" : 10.16 * mm, "offsetDistance" : 25.4 * mm});
        }
        {
            var Q0;
            Q0=makeQuery(id+"F14.boolean.opBoolean","COPY",FACE,{"derivedFrom":makeQuery(id+"F14.opExtrude","CAP_FACE",FACE,{"disambiguationData":[OSD([sQuery(id+"F12.wireOp",EDGE,"E23"),sQuery(id+"F12.wireOp",EDGE,"E24"),sQuery(id+"F12.wireOp",EDGE,"E25"),sQuery(id+"F12.wireOp",EDGE,"E26"),sQuery(id+"F12.wireOp",EDGE,"E27"),sQuery(id+"F12.wireOp",EDGE,"E28"),sQuery(id+"F12.wireOp",EDGE,"E29"),sQuery(id+"F12.wireOp",EDGE,"E30"),sQuery(id+"F12.wireOp",EDGE,"E31"),sQuery(id+"F12.wireOp",EDGE,"E32"),sQuery(id+"F12.wireOp",EDGE,"E33"),sQuery(id+"F12.wireOp",EDGE,"E34"),sQuery(id+"F12.wireOp",EDGE,"E35"),sQuery(id+"F12.wireOp",EDGE,"E36"),sQuery(id+"F12.wireOp",EDGE,"E37"),sQuery(id+"F12.wireOp",EDGE,"E38"),sQuery(id+"F12.wireOp",EDGE,"E39"),sQuery(id+"F12.wireOp",EDGE,"E40"),sQuery(id+"F12.wireOp",EDGE,"E41"),sQuery(id+"F12.wireOp",EDGE,"E42"),sQuery(id+"F12.wireOp",EDGE,"E43"),sQuery(id+"F12.wireOp",EDGE,"E44"),sQuery(id+"F12.wireOp",EDGE,"E45"),sQuery(id+"F12.wireOp",EDGE,"E46"),sQuery(id+"F12.wireOp",EDGE,"E47"),sQuery(id+"F12.wireOp",EDGE,"E48"),sQuery(id+"F12.wireOp",EDGE,"E49"),sQuery(id+"F12.wireOp",EDGE,"E50"),sQuery(id+"F12.wireOp",EDGE,"E51"),sQuery(id+"F12.wireOp",EDGE,"E52"),sQuery(id+"F12.wireOp",EDGE,"E53"),sQuery(id+"F12.wireOp",EDGE,"E54"),sQuery(id+"F12.wireOp",EDGE,"E55"),sQuery(id+"F12.wireOp",EDGE,"E56"),sQuery(id+"F12.wireOp",EDGE,"E57"),sQuery(id+"F12.wireOp",EDGE,"E58"),sQuery(id+"F12.wireOp",EDGE,"E59"),sQuery(id+"F12.wireOp",EDGE,"E60"),sQuery(id+"F12.wireOp",EDGE,"E61"),sQuery(id+"F12.wireOp",EDGE,"E62"),sQuery(id+"F12.wireOp",EDGE,"E63"),sQuery(id+"F12.wireOp",EDGE,"E64"),sQuery(id+"F12.wireOp",EDGE,"E65"),sQuery(id+"F12.wireOp",EDGE,"E66"),sQuery(id+"F12.wireOp",EDGE,"E67"),sQuery(id+"F12.wireOp",EDGE,"E68"),sQuery(id+"F12.wireOp",EDGE,"E69"),sQuery(id+"F12.wireOp",EDGE,"E70"),sQuery(id+"F12.wireOp",EDGE,"E71"),sQuery(id+"F12.wireOp",EDGE,"E72"),sQuery(id+"F12.wireOp",EDGE,"E73"),sQuery(id+"F12.wireOp",EDGE,"E74"),sQuery(id+"F12.wireOp",EDGE,"E75"),sQuery(id+"F12.wireOp",EDGE,"E76"),sQuery(id+"F12.wireOp",EDGE,"E77"),sQuery(id+"F12.wireOp",EDGE,"E78"),sQuery(id+"F12.wireOp",EDGE,"E79"),sQuery(id+"F12.wireOp",EDGE,"E80"),sQuery(id+"F12.wireOp",EDGE,"E81"),sQuery(id+"F12.wireOp",EDGE,"E82")])],"isStart":false})});
            extrude(context, id + "F15", {"entities" : qUnion([Q0]), "operationType" : NewBodyOperationType.ADD, "oppositeDirection" : true, "depth" : 25.4 * mm, "offsetDistance" : 25.4 * mm});
        }
        {
            var Q0;
            Q0=makeQuery(id+"F15.opExtrude","CAP_FACE",FACE,{"disambiguationData":[OSD([sQuery(id+"F12.wireOp",EDGE,"E23"),sQuery(id+"F12.wireOp",EDGE,"E24"),sQuery(id+"F12.wireOp",EDGE,"E25"),sQuery(id+"F12.wireOp",EDGE,"E26"),sQuery(id+"F12.wireOp",EDGE,"E27"),sQuery(id+"F12.wireOp",EDGE,"E28"),sQuery(id+"F12.wireOp",EDGE,"E29"),sQuery(id+"F12.wireOp",EDGE,"E30"),sQuery(id+"F12.wireOp",EDGE,"E31"),sQuery(id+"F12.wireOp",EDGE,"E32"),sQuery(id+"F12.wireOp",EDGE,"E33"),sQuery(id+"F12.wireOp",EDGE,"E34"),sQuery(id+"F12.wireOp",EDGE,"E35"),sQuery(id+"F12.wireOp",EDGE,"E36"),sQuery(id+"F12.wireOp",EDGE,"E37"),sQuery(id+"F12.wireOp",EDGE,"E38"),sQuery(id+"F12.wireOp",EDGE,"E39"),sQuery(id+"F12.wireOp",EDGE,"E40"),sQuery(id+"F12.wireOp",EDGE,"E41"),sQuery(id+"F12.wireOp",EDGE,"E42"),sQuery(id+"F12.wireOp",EDGE,"E43"),sQuery(id+"F12.wireOp",EDGE,"E44"),sQuery(id+"F12.wireOp",EDGE,"E45"),sQuery(id+"F12.wireOp",EDGE,"E46"),sQuery(id+"F12.wireOp",EDGE,"E47"),sQuery(id+"F12.wireOp",EDGE,"E48"),sQuery(id+"F12.wireOp",EDGE,"E49"),sQuery(id+"F12.wireOp",EDGE,"E50"),sQuery(id+"F12.wireOp",EDGE,"E51"),sQuery(id+"F12.wireOp",EDGE,"E52"),sQuery(id+"F12.wireOp",EDGE,"E53"),sQuery(id+"F12.wireOp",EDGE,"E54"),sQuery(id+"F12.wireOp",EDGE,"E55"),sQuery(id+"F12.wireOp",EDGE,"E56"),sQuery(id+"F12.wireOp",EDGE,"E57"),sQuery(id+"F12.wireOp",EDGE,"E58"),sQuery(id+"F12.wireOp",EDGE,"E59"),sQuery(id+"F12.wireOp",EDGE,"E60"),sQuery(id+"F12.wireOp",EDGE,"E61"),sQuery(id+"F12.wireOp",EDGE,"E62"),sQuery(id+"F12.wireOp",EDGE,"E63"),sQuery(id+"F12.wireOp",EDGE,"E64"),sQuery(id+"F12.wireOp",EDGE,"E65"),sQuery(id+"F12.wireOp",EDGE,"E66"),sQuery(id+"F12.wireOp",EDGE,"E67"),sQuery(id+"F12.wireOp",EDGE,"E68"),sQuery(id+"F12.wireOp",EDGE,"E69"),sQuery(id+"F12.wireOp",EDGE,"E70"),sQuery(id+"F12.wireOp",EDGE,"E71"),sQuery(id+"F12.wireOp",EDGE,"E72"),sQuery(id+"F12.wireOp",EDGE,"E73"),sQuery(id+"F12.wireOp",EDGE,"E74"),sQuery(id+"F12.wireOp",EDGE,"E75"),sQuery(id+"F12.wireOp",EDGE,"E76"),sQuery(id+"F12.wireOp",EDGE,"E77"),sQuery(id+"F12.wireOp",EDGE,"E78"),sQuery(id+"F12.wireOp",EDGE,"E79"),sQuery(id+"F12.wireOp",EDGE,"E80"),sQuery(id+"F12.wireOp",EDGE,"E81"),sQuery(id+"F12.wireOp",EDGE,"E82")])],"isStart":false});
            extrude(context, id + "F16", {"entities" : qUnion([Q0]), "operationType" : NewBodyOperationType.REMOVE, "oppositeDirection" : true, "depth" : 6.35 * mm, "offsetDistance" : 25.4 * mm});
        }
        {
            var Q0;
            Q0=makeQuery(id+"F14.boolean.opBoolean","COPY",FACE,{"derivedFrom":makeQuery(id+"F14.opExtrude","CAP_FACE",FACE,{"disambiguationData":[OSD([sQuery(id+"F12.wireOp",EDGE,"E23"),sQuery(id+"F12.wireOp",EDGE,"E24"),sQuery(id+"F12.wireOp",EDGE,"E25"),sQuery(id+"F12.wireOp",EDGE,"E26"),sQuery(id+"F12.wireOp",EDGE,"E27"),sQuery(id+"F12.wireOp",EDGE,"E28"),sQuery(id+"F12.wireOp",EDGE,"E29"),sQuery(id+"F12.wireOp",EDGE,"E30"),sQuery(id+"F12.wireOp",EDGE,"E31"),sQuery(id+"F12.wireOp",EDGE,"E32"),sQuery(id+"F12.wireOp",EDGE,"E33"),sQuery(id+"F12.wireOp",EDGE,"E34"),sQuery(id+"F12.wireOp",EDGE,"E35"),sQuery(id+"F12.wireOp",EDGE,"E36"),sQuery(id+"F12.wireOp",EDGE,"E37"),sQuery(id+"F12.wireOp",EDGE,"E38"),sQuery(id+"F12.wireOp",EDGE,"E39"),sQuery(id+"F12.wireOp",EDGE,"E40"),sQuery(id+"F12.wireOp",EDGE,"E41"),sQuery(id+"F12.wireOp",EDGE,"E42"),sQuery(id+"F12.wireOp",EDGE,"E43"),sQuery(id+"F12.wireOp",EDGE,"E44"),sQuery(id+"F12.wireOp",EDGE,"E45"),sQuery(id+"F12.wireOp",EDGE,"E46"),sQuery(id+"F12.wireOp",EDGE,"E47"),sQuery(id+"F12.wireOp",EDGE,"E48"),sQuery(id+"F12.wireOp",EDGE,"E49"),sQuery(id+"F12.wireOp",EDGE,"E50"),sQuery(id+"F12.wireOp",EDGE,"E51"),sQuery(id+"F12.wireOp",EDGE,"E52"),sQuery(id+"F12.wireOp",EDGE,"E53"),sQuery(id+"F12.wireOp",EDGE,"E54"),sQuery(id+"F12.wireOp",EDGE,"E55"),sQuery(id+"F12.wireOp",EDGE,"E56"),sQuery(id+"F12.wireOp",EDGE,"E57"),sQuery(id+"F12.wireOp",EDGE,"E58"),sQuery(id+"F12.wireOp",EDGE,"E59"),sQuery(id+"F12.wireOp",EDGE,"E60"),sQuery(id+"F12.wireOp",EDGE,"E61"),sQuery(id+"F12.wireOp",EDGE,"E62"),sQuery(id+"F12.wireOp",EDGE,"E63"),sQuery(id+"F12.wireOp",EDGE,"E64"),sQuery(id+"F12.wireOp",EDGE,"E65"),sQuery(id+"F12.wireOp",EDGE,"E66"),sQuery(id+"F12.wireOp",EDGE,"E67"),sQuery(id+"F12.wireOp",EDGE,"E68"),sQuery(id+"F12.wireOp",EDGE,"E69"),sQuery(id+"F12.wireOp",EDGE,"E70"),sQuery(id+"F12.wireOp",EDGE,"E71"),sQuery(id+"F12.wireOp",EDGE,"E72"),sQuery(id+"F12.wireOp",EDGE,"E73"),sQuery(id+"F12.wireOp",EDGE,"E74"),sQuery(id+"F12.wireOp",EDGE,"E75"),sQuery(id+"F12.wireOp",EDGE,"E76"),sQuery(id+"F12.wireOp",EDGE,"E77"),sQuery(id+"F12.wireOp",EDGE,"E78"),sQuery(id+"F12.wireOp",EDGE,"E79"),sQuery(id+"F12.wireOp",EDGE,"E80"),sQuery(id+"F12.wireOp",EDGE,"E81"),sQuery(id+"F12.wireOp",EDGE,"E82")])],"isStart":false})});
            extrude(context, id + "F17", {"entities" : qUnion([Q0]), "operationType" : NewBodyOperationType.REMOVE, "oppositeDirection" : true, "depth" : 3.05 * mm, "offsetDistance" : 25.4 * mm});
        }
        {
            var Q0;
            Q0=makeQuery(id+"F17.boolean.opBoolean","COPY",FACE,{"derivedFrom":makeQuery(id+"F17.opExtrude","CAP_FACE",FACE,{"disambiguationData":[OSD([sQuery(id+"F12.wireOp",EDGE,"E23"),sQuery(id+"F12.wireOp",EDGE,"E24"),sQuery(id+"F12.wireOp",EDGE,"E25"),sQuery(id+"F12.wireOp",EDGE,"E26"),sQuery(id+"F12.wireOp",EDGE,"E27"),sQuery(id+"F12.wireOp",EDGE,"E28"),sQuery(id+"F12.wireOp",EDGE,"E29"),sQuery(id+"F12.wireOp",EDGE,"E30"),sQuery(id+"F12.wireOp",EDGE,"E31"),sQuery(id+"F12.wireOp",EDGE,"E32"),sQuery(id+"F12.wireOp",EDGE,"E33"),sQuery(id+"F12.wireOp",EDGE,"E34"),sQuery(id+"F12.wireOp",EDGE,"E35"),sQuery(id+"F12.wireOp",EDGE,"E36"),sQuery(id+"F12.wireOp",EDGE,"E37"),sQuery(id+"F12.wireOp",EDGE,"E38"),sQuery(id+"F12.wireOp",EDGE,"E39"),sQuery(id+"F12.wireOp",EDGE,"E40"),sQuery(id+"F12.wireOp",EDGE,"E41"),sQuery(id+"F12.wireOp",EDGE,"E42"),sQuery(id+"F12.wireOp",EDGE,"E43"),sQuery(id+"F12.wireOp",EDGE,"E44"),sQuery(id+"F12.wireOp",EDGE,"E45"),sQuery(id+"F12.wireOp",EDGE,"E46"),sQuery(id+"F12.wireOp",EDGE,"E47"),sQuery(id+"F12.wireOp",EDGE,"E48"),sQuery(id+"F12.wireOp",EDGE,"E49"),sQuery(id+"F12.wireOp",EDGE,"E50"),sQuery(id+"F12.wireOp",EDGE,"E51"),sQuery(id+"F12.wireOp",EDGE,"E52"),sQuery(id+"F12.wireOp",EDGE,"E53"),sQuery(id+"F12.wireOp",EDGE,"E54"),sQuery(id+"F12.wireOp",EDGE,"E55"),sQuery(id+"F12.wireOp",EDGE,"E56"),sQuery(id+"F12.wireOp",EDGE,"E57"),sQuery(id+"F12.wireOp",EDGE,"E58"),sQuery(id+"F12.wireOp",EDGE,"E59"),sQuery(id+"F12.wireOp",EDGE,"E60"),sQuery(id+"F12.wireOp",EDGE,"E61"),sQuery(id+"F12.wireOp",EDGE,"E62"),sQuery(id+"F12.wireOp",EDGE,"E63"),sQuery(id+"F12.wireOp",EDGE,"E64"),sQuery(id+"F12.wireOp",EDGE,"E65"),sQuery(id+"F12.wireOp",EDGE,"E66"),sQuery(id+"F12.wireOp",EDGE,"E67"),sQuery(id+"F12.wireOp",EDGE,"E68"),sQuery(id+"F12.wireOp",EDGE,"E69"),sQuery(id+"F12.wireOp",EDGE,"E70"),sQuery(id+"F12.wireOp",EDGE,"E71"),sQuery(id+"F12.wireOp",EDGE,"E72"),sQuery(id+"F12.wireOp",EDGE,"E73"),sQuery(id+"F12.wireOp",EDGE,"E74"),sQuery(id+"F12.wireOp",EDGE,"E75"),sQuery(id+"F12.wireOp",EDGE,"E76"),sQuery(id+"F12.wireOp",EDGE,"E77"),sQuery(id+"F12.wireOp",EDGE,"E78"),sQuery(id+"F12.wireOp",EDGE,"E79"),sQuery(id+"F12.wireOp",EDGE,"E80"),sQuery(id+"F12.wireOp",EDGE,"E81"),sQuery(id+"F12.wireOp",EDGE,"E82")])],"isStart":false})});
            extrude(context, id + "F18", {"entities" : qUnion([Q0]), "operationType" : NewBodyOperationType.REMOVE, "oppositeDirection" : true, "depth" : 0.25 * mm, "offsetDistance" : 25.4 * mm});
        }
    });
